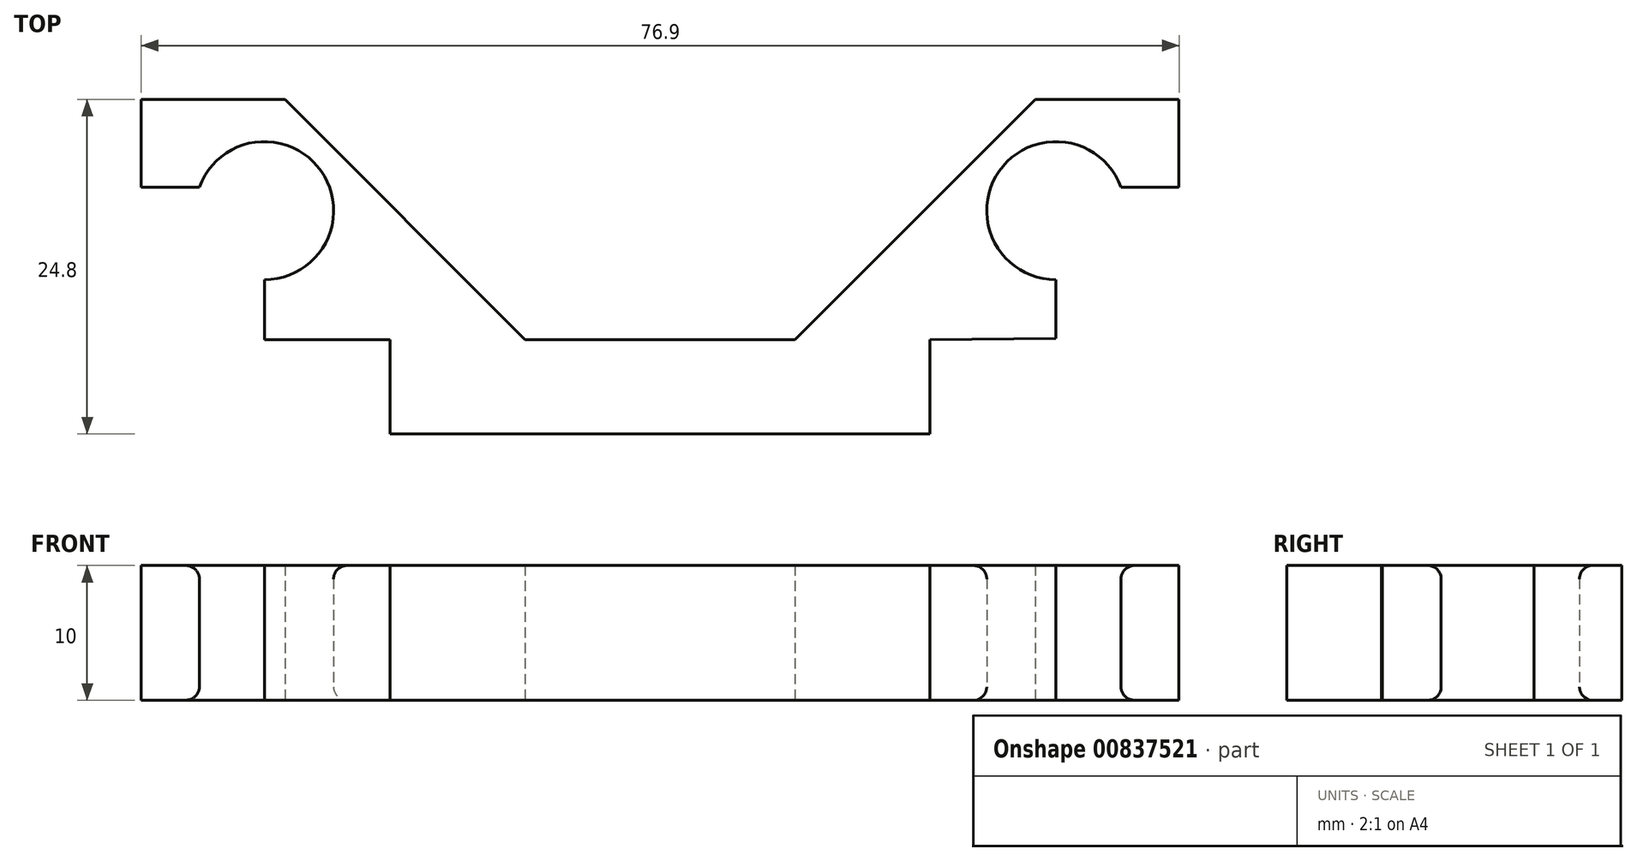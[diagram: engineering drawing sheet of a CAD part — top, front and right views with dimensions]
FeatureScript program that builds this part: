
annotation { "Feature Type Name" : "Feature", "Feature Type Description" : "" }
export const myFeature = defineFeature(function(context is Context, id is Id, definition is map)
    precondition{}
    {
        {
            var Q0;
            Q0=qCreatedBy(makeId("Top.planeOp"),FACE);
            var sketch = newSketch(context, id + "F0", { "sketchPlane" : qUnion([Q0])});
            skLineSegment(sketch, "E0.bottom", {"start": v(-11.53, -17.8) * mm, "end": v(28.47, -17.8) * mm});
            skLineSegment(sketch, "E0.top", {"start": v(-11.53, -24.8) * mm, "end": v(28.47, -24.8) * mm});
            skLineSegment(sketch, "E0.left", {"start": v(-11.53, -17.8) * mm, "end": v(-11.53, -24.8) * mm});
            skLineSegment(sketch, "E0.right", {"start": v(28.47, -17.8) * mm, "end": v(28.47, -24.8) * mm});
            skPoint(sketch, "E1", {"position": v(8.47, -17.8) * mm});
            skPoint(sketch, "E2", {"position": v(8.47, -24.8) * mm});
            skLineSegment(sketch, "E3", {"start": v(8.47, -17.8) * mm, "end": v(8.47, -24.8) * mm});
            skPoint(sketch, "E4", {"position": v(-1.53, -17.8) * mm});
            skPoint(sketch, "E5", {"position": v(18.47, -17.8) * mm});
            skLineSegment(sketch, "E6", {"start": v(-1.53, -17.8) * mm, "end": v(-19.34, 0) * mm});
            skLineSegment(sketch, "E7", {"start": v(18.47, -17.8) * mm, "end": v(36.27, 0) * mm});
            skPoint(sketch, "E8", {"position": v(-11.53, -7.8) * mm});
            skPoint(sketch, "E9", {"position": v(28.47, -7.8) * mm});
            skLineSegment(sketch, "E10", {"start": v(-25.98, 0) * mm, "end": v(-19.34, 0) * mm});
            skPoint(sketch, "E11", {"position": v(8.47, 0) * mm});
            skPoint(sketch, "E12", {"position": v(-20.86, 0) * mm});
            skPoint(sketch, "E13", {"position": v(37.8, 0) * mm});
            skPoint(sketch, "E14", {"position": v(-20.86, -8.25) * mm});
            skPoint(sketch, "E15", {"position": v(37.8, -8.25) * mm});
            skArc(sketch, "E16", {"start": v(-20.86, -13.38) * mm, "mid": v(-16.66, -5.3) * mm, "end": v(-25.67, -6.5) * mm});
            skArc(sketch, "E17", {"start": v(42.6, -6.5) * mm, "mid": v(33.6, -5.3) * mm, "end": v(37.8, -13.38) * mm});
            skLineSegment(sketch, "E18", {"start": v(-29.98, 0) * mm, "end": v(-19.34, 0) * mm});
            skLineSegment(sketch, "E19", {"start": v(-29.98, 0) * mm, "end": v(-29.98, -6.5) * mm});
            skLineSegment(sketch, "E20", {"start": v(46.92, 0) * mm, "end": v(46.92, -6.5) * mm});
            skLineSegment(sketch, "E21", {"start": v(-29.98, -6.5) * mm, "end": v(-25.67, -6.5) * mm});
            skLineSegment(sketch, "E22", {"start": v(46.92, -6.5) * mm, "end": v(42.6, -6.5) * mm});
            skLineSegment(sketch, "E23.trimOffspring", {"start": v(36.27, 0) * mm, "end": v(46.92, 0) * mm});
            skLineSegment(sketch, "E24.trimOffspring", {"start": v(36.27, 0) * mm, "end": v(42.92, 0) * mm});
            skLineSegment(sketch, "E25.trimOffspring", {"start": v(-20.86, -13.38) * mm, "end": v(-20.86, -16.5) * mm});
            skLineSegment(sketch, "E26.trimOffspring", {"start": v(37.8, -13.38) * mm, "end": v(37.8, -17.72) * mm});
            skLineSegment(sketch, "E27", {"start": v(-20.86, -13.38) * mm, "end": v(-20.86, -17.8) * mm});
            skLineSegment(sketch, "E28", {"start": v(-20.86, -17.8) * mm, "end": v(-11.53, -17.8) * mm});
            skLineSegment(sketch, "E29", {"start": v(28.47, -17.8) * mm, "end": v(37.8, -17.72) * mm});
            skSolve(sketch);
        }
        {
            var Q0;
            Q0 = qSketchRegion(id + "F0", true);
            extrude(context, id + "F1", {"entities" : qUnion([Q0]), "depth" : 10 * mm, "offsetDistance" : 25 * mm});
        }
        {
            var Q0;
            Q0=makeQuery(id+"F1.opExtrude","CAP_EDGE",EDGE,{"disambiguationData":[OSD([sQuery(id+"F0.wireOp",EDGE,"E16")])],"isStart":false});
            fillet(context, id + "F2", {"entities" : qUnion([Q0]), "radius" : 1 * mm, "tangentPropagation" : true, "allowEdgeOverflow" : false});
        }
        {
            var Q0;
            Q0=makeQuery(id+"F1.opExtrude","CAP_EDGE",EDGE,{"disambiguationData":[OSD([sQuery(id+"F0.wireOp",EDGE,"E17")])],"isStart":false});
            var Q1;
            Q1=makeQuery(id+"F1.opExtrude","CAP_EDGE",EDGE,{"disambiguationData":[OSD([sQuery(id+"F0.wireOp",EDGE,"E16")])],"isStart":true});
            var Q2;
            Q2=makeQuery(id+"F1.opExtrude","CAP_EDGE",EDGE,{"disambiguationData":[OSD([sQuery(id+"F0.wireOp",EDGE,"E17")])],"isStart":true});
            fillet(context, id + "F3", {"entities" : qUnion([Q0, Q1, Q2]), "radius" : 1 * mm, "tangentPropagation" : true, "allowEdgeOverflow" : false});
        }
    });
